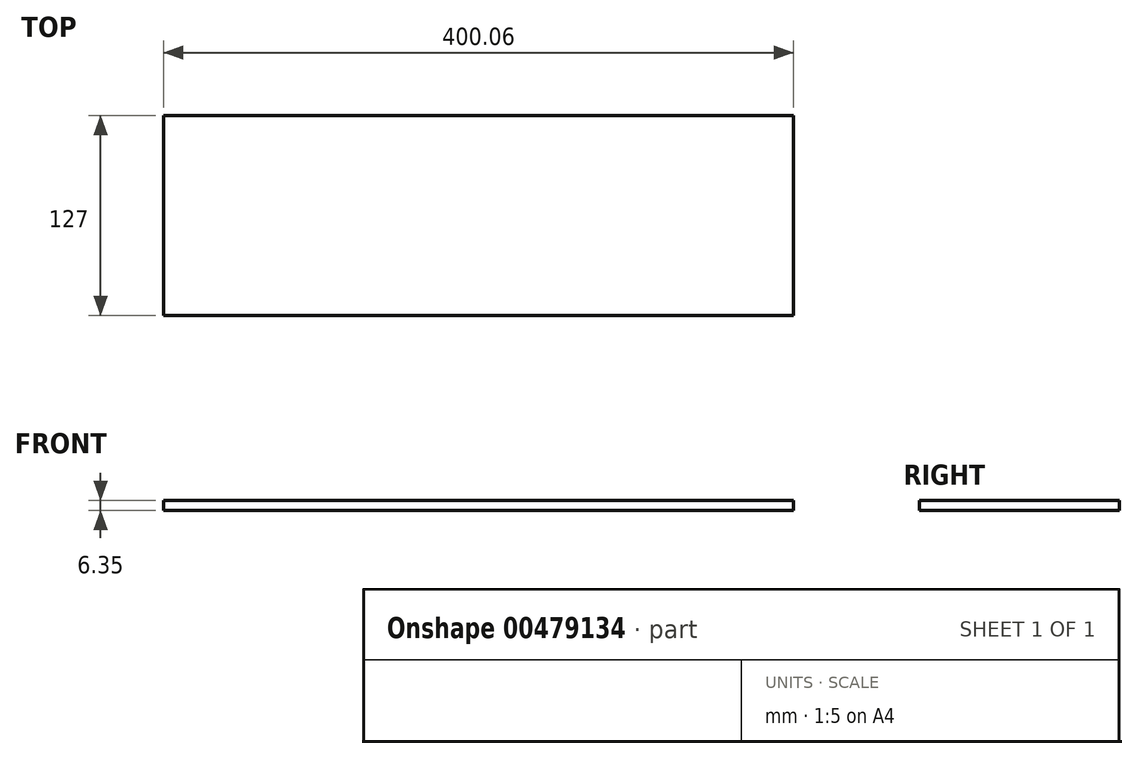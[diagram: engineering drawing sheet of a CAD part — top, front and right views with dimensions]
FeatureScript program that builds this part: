
annotation { "Feature Type Name" : "Feature", "Feature Type Description" : "" }
export const myFeature = defineFeature(function(context is Context, id is Id, definition is map)
    precondition{}
    {
        {
            var Q0;
            Q0=qCreatedBy(makeId("Top.planeOp"),FACE);
            var sketch = newSketch(context, id + "F0", { "sketchPlane" : qUnion([Q0])});
            skLineSegment(sketch, "E0.bottom", {"start": v(200.02, 63.5) * mm, "end": v(-200.03, 63.5) * mm});
            skLineSegment(sketch, "E0.top", {"start": v(200.03, -63.5) * mm, "end": v(-200.02, -63.5) * mm});
            skLineSegment(sketch, "E0.left", {"start": v(200.02, 63.5) * mm, "end": v(200.03, -63.5) * mm});
            skLineSegment(sketch, "E0.right", {"start": v(-200.03, 63.5) * mm, "end": v(-200.02, -63.5) * mm});
            skPoint(sketch, "E0.middle", {"position": v(0, 0) * mm});
            skSolve(sketch);
        }
        {
            var Q0;
            Q0 = qSketchRegion(id + "F0", true);
            extrude(context, id + "F1", {"entities" : qUnion([Q0]), "depth" : 6.35 * mm});
        }
    });
